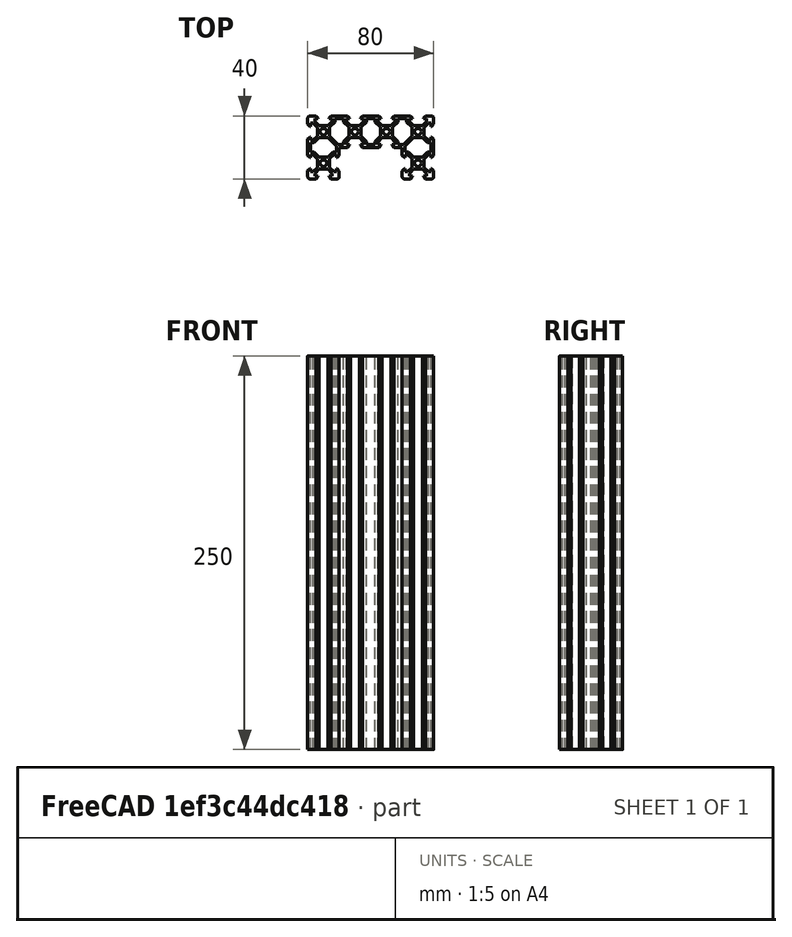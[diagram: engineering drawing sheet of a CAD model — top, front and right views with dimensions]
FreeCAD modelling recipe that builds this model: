
FCSTD DOCUMENT  (FreeCAD 0.15R4671 (Git))
Label: c-beam profile
License: All rights reserved
LicenseURL: http://en.wikipedia.org/wiki/All_rights_reserved
objects: Sketcher::SketchObject×1, Part::Extrusion×1
note: 2 computed .brp shape members not serialized (recipe doc carries the construction recipe); baked Part::Feature solids carry a one-line shape summary decoded from their .brp

FEATURE [Sketcher::SketchObject] Sketch
  sketch-geometry (252):
    g0: LineSegment StartX=57.3 StartY=-18.2 StartZ=0 EndX=57.3 EndY=-16.239 EndZ=0
    g1: LineSegment StartX=57.3 StartY=-16.239 StartZ=0 EndX=53.9 EndY=-12.839 EndZ=0
    g2: LineSegment StartX=53.9 StartY=-12.839 StartZ=0 EndX=53.9 EndY=-7.161 EndZ=0
    g3: LineSegment StartX=53.9 StartY=-7.161 StartZ=0 EndX=57.3 EndY=-3.761 EndZ=0
    g4: LineSegment StartX=57.3 StartY=-3.761 StartZ=0 EndX=57.3 EndY=-1.8 EndZ=0
    g5: LineSegment StartX=57.3 StartY=-1.8 StartZ=0 EndX=60 EndY=-1.8 EndZ=0
    g6: LineSegment StartX=60 StartY=-1.8 StartZ=0 EndX=62.7 EndY=-1.8 EndZ=0
    g7: LineSegment StartX=62.7 StartY=-1.8 StartZ=0 EndX=62.7 EndY=-3.761 EndZ=0
    g8: LineSegment StartX=62.7 StartY=-3.761 StartZ=0 EndX=66.1 EndY=-7.161 EndZ=0
    g9: LineSegment StartX=66.1 StartY=-7.161 StartZ=0 EndX=66.1 EndY=-12.839 EndZ=0
    g10: LineSegment StartX=66.1 StartY=-12.839 StartZ=0 EndX=60.6708 EndY=-18.2 EndZ=0
    g11: LineSegment StartX=60.6708 StartY=-18.2 StartZ=0 EndX=60 EndY=-18.2 EndZ=0
    g12: LineSegment StartX=60 StartY=-18.2 StartZ=0 EndX=57.3 EndY=-18.2 EndZ=0
    g13: LineSegment StartX=20 StartY=-18.2 StartZ=0 EndX=19.3292 EndY=-18.2 EndZ=0
    g14: LineSegment StartX=19.3292 StartY=-18.2 StartZ=0 EndX=13.9 EndY=-12.839 EndZ=0
    g15: LineSegment StartX=13.9 StartY=-12.839 StartZ=0 EndX=13.9 EndY=-7.161 EndZ=0
    g16: LineSegment StartX=13.9 StartY=-7.161 StartZ=0 EndX=17.3 EndY=-3.761 EndZ=0
    g17: LineSegment StartX=17.3 StartY=-3.761 StartZ=0 EndX=17.3 EndY=-1.8 EndZ=0
    g18: LineSegment StartX=17.3 StartY=-1.8 StartZ=0 EndX=20 EndY=-1.8 EndZ=0
    g19: LineSegment StartX=20 StartY=-1.8 StartZ=0 EndX=22.7 EndY=-1.8 EndZ=0
    g20: LineSegment StartX=22.7 StartY=-1.8 StartZ=0 EndX=22.7 EndY=-3.761 EndZ=0
    g21: LineSegment StartX=22.7 StartY=-3.761 StartZ=0 EndX=26.1 EndY=-7.161 EndZ=0
    g22: LineSegment StartX=26.1 StartY=-7.161 StartZ=0 EndX=26.1 EndY=-12.839 EndZ=0
    g23: LineSegment StartX=26.1 StartY=-12.839 StartZ=0 EndX=22.7 EndY=-16.239 EndZ=0
    g24: LineSegment StartX=22.7 StartY=-16.239 StartZ=0 EndX=22.7 EndY=-18.2 EndZ=0
    g25: LineSegment StartX=22.7 StartY=-18.2 StartZ=0 EndX=20 EndY=-18.2 EndZ=0
    g26: ArcOfCircle CenterX=1.5 CenterY=-1.5 CenterZ=0 NormalX=0 NormalY=0 NormalZ=1 Radius=1.5 StartAngle=1.5708 EndAngle=3.14159
    g27: LineSegment StartX=5.114 StartY=0 StartZ=0 EndX=1.5 EndY=0 EndZ=0
    g28: LineSegment StartX=0 StartY=-1.5 StartZ=0 EndX=0 EndY=-5.2509 EndZ=0
    g29: LineSegment StartX=0 StartY=-5.2509 StartZ=0 EndX=1.3621 EndY=-6.613 EndZ=0
    g30: LineSegment StartX=1.3621 StartY=-6.613 StartZ=0 EndX=1.6631 EndY=-6.613 EndZ=0
    g31: LineSegment StartX=1.6631 StartY=-6.613 StartZ=0 EndX=1.6631 EndY=-4.5 EndZ=0
    g32: LineSegment StartX=1.6631 StartY=-4.5 StartZ=0 EndX=3.3021 EndY=-4.5 EndZ=0
    g33: LineSegment StartX=3.3021 StartY=-4.5 StartZ=0 EndX=6.1 EndY=-7.2979 EndZ=0
    g34: LineSegment StartX=6.1 StartY=-7.2979 StartZ=0 EndX=6.1 EndY=-12.7021 EndZ=0
    g35: LineSegment StartX=6.1 StartY=-12.7021 StartZ=0 EndX=3.3021 EndY=-15.5 EndZ=0
    g36: LineSegment StartX=3.3021 StartY=-15.5 StartZ=0 EndX=1.6631 EndY=-15.5 EndZ=0
    g37: LineSegment StartX=1.6631 StartY=-15.5 StartZ=0 EndX=1.6631 EndY=-13.387 EndZ=0
    g38: LineSegment StartX=1.6631 StartY=-13.387 StartZ=0 EndX=1.3621 EndY=-13.387 EndZ=0
    g39: LineSegment StartX=1.3621 StartY=-13.387 StartZ=0 EndX=0 EndY=-14.7491 EndZ=0
    g40: LineSegment StartX=0 StartY=-14.7491 StartZ=0 EndX=0 EndY=-25.2509 EndZ=0
    g41: LineSegment StartX=0 StartY=-25.2509 StartZ=0 EndX=1.3621 EndY=-26.613 EndZ=0
    g42: LineSegment StartX=1.3621 StartY=-26.613 StartZ=0 EndX=1.6631 EndY=-26.613 EndZ=0
    g43: LineSegment StartX=1.6631 StartY=-26.613 StartZ=0 EndX=1.6631 EndY=-24.5 EndZ=0
    g44: LineSegment StartX=1.6631 StartY=-24.5 StartZ=0 EndX=3.3021 EndY=-24.5 EndZ=0
    g45: LineSegment StartX=3.3021 StartY=-24.5 StartZ=0 EndX=6.1 EndY=-27.2979 EndZ=0
    g46: LineSegment StartX=6.1 StartY=-27.2979 StartZ=0 EndX=6.1 EndY=-32.7021 EndZ=0
    g47: LineSegment StartX=6.1 StartY=-32.7021 StartZ=0 EndX=3.3021 EndY=-35.5 EndZ=0
    g48: LineSegment StartX=3.3021 StartY=-35.5 StartZ=0 EndX=1.6631 EndY=-35.5 EndZ=0
    g49: LineSegment StartX=1.6631 StartY=-35.5 StartZ=0 EndX=1.6631 EndY=-33.387 EndZ=0
    g50: LineSegment StartX=1.6631 StartY=-33.387 StartZ=0 EndX=1.3621 EndY=-33.387 EndZ=0
    g51: LineSegment StartX=1.3621 StartY=-33.387 StartZ=0 EndX=0 EndY=-34.7491 EndZ=0
    g52: LineSegment StartX=0 StartY=-34.7491 StartZ=0 EndX=0 EndY=-38.5 EndZ=0
    g53: ArcOfCircle CenterX=1.5 CenterY=-38.5 CenterZ=0 NormalX=0 NormalY=0 NormalZ=1 Radius=1.5 StartAngle=3.14159 EndAngle=4.71239
    g54: LineSegment StartX=1.5 StartY=-40 StartZ=0 EndX=5.114 EndY=-40 EndZ=0
    g55: LineSegment StartX=5.114 StartY=-40 StartZ=0 EndX=6.613 EndY=-38.501 EndZ=0
    g56: LineSegment StartX=6.613 StartY=-38.501 StartZ=0 EndX=6.613 EndY=-38.2 EndZ=0
    g57: LineSegment StartX=6.613 StartY=-38.2 StartZ=0 EndX=4.5 EndY=-38.2 EndZ=0
    g58: LineSegment StartX=4.5 StartY=-38.2 StartZ=0 EndX=4.5 EndY=-36.561 EndZ=0
    g59: LineSegment StartX=4.5 StartY=-36.561 StartZ=0 EndX=7.161 EndY=-33.9 EndZ=0
    g60: LineSegment StartX=7.161 StartY=-33.9 StartZ=0 EndX=12.839 EndY=-33.9 EndZ=0
    g61: LineSegment StartX=12.839 StartY=-33.9 StartZ=0 EndX=15.5 EndY=-36.561 EndZ=0
    g62: LineSegment StartX=15.5 StartY=-36.561 StartZ=0 EndX=15.5 EndY=-38.2 EndZ=0
    g63: LineSegment StartX=15.5 StartY=-38.2 StartZ=0 EndX=13.387 EndY=-38.2 EndZ=0
    g64: LineSegment StartX=13.387 StartY=-38.2 StartZ=0 EndX=13.387 EndY=-38.501 EndZ=0
    g65: LineSegment StartX=13.387 StartY=-38.501 StartZ=0 EndX=14.886 EndY=-40 EndZ=0
    g66: LineSegment StartX=14.886 StartY=-40 StartZ=0 EndX=18.5 EndY=-40 EndZ=0
    g67: ArcOfCircle CenterX=18.5 CenterY=-38.5 CenterZ=0 NormalX=0 NormalY=0 NormalZ=1 Radius=1.5 StartAngle=4.71239 EndAngle=6.28319
    g68: LineSegment StartX=20 StartY=-38.5 StartZ=0 EndX=20 EndY=-34.886 EndZ=0
    g69: LineSegment StartX=20 StartY=-34.886 StartZ=0 EndX=18.501 EndY=-33.387 EndZ=0
    g70: LineSegment StartX=18.501 StartY=-33.387 StartZ=0 EndX=18.2 EndY=-33.387 EndZ=0
    g71: LineSegment StartX=18.2 StartY=-33.387 StartZ=0 EndX=18.2 EndY=-35.5 EndZ=0
    g72: LineSegment StartX=18.2 StartY=-35.5 StartZ=0 EndX=16.561 EndY=-35.5 EndZ=0
    g73: LineSegment StartX=16.561 StartY=-35.5 StartZ=0 EndX=13.9 EndY=-32.839 EndZ=0
    g74: LineSegment StartX=13.9 StartY=-32.839 StartZ=0 EndX=13.9 EndY=-27.161 EndZ=0
    g75: LineSegment StartX=13.9 StartY=-27.161 StartZ=0 EndX=16.561 EndY=-24.5 EndZ=0
    g76: LineSegment StartX=16.561 StartY=-24.5 StartZ=0 EndX=18.2 EndY=-24.5 EndZ=0
    g77: LineSegment StartX=18.2 StartY=-24.5 StartZ=0 EndX=18.2 EndY=-26.613 EndZ=0
    g78: LineSegment StartX=18.2 StartY=-26.613 StartZ=0 EndX=18.501 EndY=-26.613 EndZ=0
    g79: LineSegment StartX=18.501 StartY=-26.613 StartZ=0 EndX=20 EndY=-25.114 EndZ=0
    g80: LineSegment StartX=20 StartY=-25.114 StartZ=0 EndX=20 EndY=-20 EndZ=0
    g81: LineSegment StartX=20 StartY=-20 StartZ=0 EndX=25.114 EndY=-20 EndZ=0
    g82: LineSegment StartX=25.114 StartY=-20 StartZ=0 EndX=26.613 EndY=-18.501 EndZ=0
    g83: LineSegment StartX=26.613 StartY=-18.501 StartZ=0 EndX=26.613 EndY=-18.2 EndZ=0
    g84: LineSegment StartX=26.613 StartY=-18.2 StartZ=0 EndX=24.5 EndY=-18.2 EndZ=0
    g85: LineSegment StartX=24.5 StartY=-18.2 StartZ=0 EndX=24.5 EndY=-16.561 EndZ=0
    g86: LineSegment StartX=24.5 StartY=-16.561 StartZ=0 EndX=27.161 EndY=-13.9 EndZ=0
    g87: LineSegment StartX=27.161 StartY=-13.9 StartZ=0 EndX=32.839 EndY=-13.9 EndZ=0
    g88: LineSegment StartX=32.839 StartY=-13.9 StartZ=0 EndX=35.5 EndY=-16.561 EndZ=0
    g89: LineSegment StartX=35.5 StartY=-16.561 StartZ=0 EndX=35.5 EndY=-18.2 EndZ=0
    g90: LineSegment StartX=35.5 StartY=-18.2 StartZ=0 EndX=33.387 EndY=-18.2 EndZ=0
    g91: LineSegment StartX=33.387 StartY=-18.2 StartZ=0 EndX=33.387 EndY=-18.501 EndZ=0
    g92: LineSegment StartX=33.387 StartY=-18.501 StartZ=0 EndX=34.886 EndY=-20 EndZ=0
    g93: LineSegment StartX=34.886 StartY=-20 StartZ=0 EndX=45.114 EndY=-20 EndZ=0
    g94: LineSegment StartX=45.114 StartY=-20 StartZ=0 EndX=46.613 EndY=-18.501 EndZ=0
    g95: LineSegment StartX=46.613 StartY=-18.501 StartZ=0 EndX=46.613 EndY=-18.2 EndZ=0
    g96: LineSegment StartX=46.613 StartY=-18.2 StartZ=0 EndX=44.5 EndY=-18.2 EndZ=0
    g97: LineSegment StartX=44.5 StartY=-18.2 StartZ=0 EndX=44.5 EndY=-16.561 EndZ=0
    g98: LineSegment StartX=44.5 StartY=-16.561 StartZ=0 EndX=47.161 EndY=-13.9 EndZ=0
    g99: LineSegment StartX=47.161 StartY=-13.9 StartZ=0 EndX=52.839 EndY=-13.9 EndZ=0
    g100: LineSegment StartX=52.839 StartY=-13.9 StartZ=0 EndX=55.5 EndY=-16.561 EndZ=0
    g101: LineSegment StartX=55.5 StartY=-16.561 StartZ=0 EndX=55.5 EndY=-18.2 EndZ=0
    g102: LineSegment StartX=55.5 StartY=-18.2 StartZ=0 EndX=53.387 EndY=-18.2 EndZ=0
    g103: LineSegment StartX=53.387 StartY=-18.2 StartZ=0 EndX=53.387 EndY=-18.501 EndZ=0
    g104: LineSegment StartX=53.387 StartY=-18.501 StartZ=0 EndX=54.886 EndY=-20 EndZ=0
    g105: LineSegment StartX=54.886 StartY=-20 StartZ=0 EndX=54.8918 EndY=-20 EndZ=0
    g106: LineSegment StartX=54.8918 StartY=-20 StartZ=0 EndX=55.1918 EndY=-19.9988 EndZ=0
    g107: LineSegment StartX=55.1918 StartY=-19.9988 StartZ=0 EndX=60 EndY=-20 EndZ=0
    g108: LineSegment StartX=60 StartY=-20 StartZ=0 EndX=60 EndY=-25.114 EndZ=0
    g109: LineSegment StartX=60 StartY=-25.114 StartZ=0 EndX=61.499 EndY=-26.613 EndZ=0
    g110: LineSegment StartX=61.499 StartY=-26.613 StartZ=0 EndX=61.8 EndY=-26.613 EndZ=0
    g111: LineSegment StartX=61.8 StartY=-26.613 StartZ=0 EndX=61.8 EndY=-24.5 EndZ=0
    g112: LineSegment StartX=61.8 StartY=-24.5 StartZ=0 EndX=63.439 EndY=-24.5 EndZ=0
    g113: LineSegment StartX=63.439 StartY=-24.5 StartZ=0 EndX=66.1 EndY=-27.161 EndZ=0
    g114: LineSegment StartX=66.1 StartY=-27.161 StartZ=0 EndX=66.1 EndY=-32.839 EndZ=0
    g115: LineSegment StartX=66.1 StartY=-32.839 StartZ=0 EndX=63.439 EndY=-35.5 EndZ=0
    g116: LineSegment StartX=63.439 StartY=-35.5 StartZ=0 EndX=61.8 EndY=-35.5 EndZ=0
    g117: LineSegment StartX=61.8 StartY=-35.5 StartZ=0 EndX=61.8 EndY=-33.387 EndZ=0
    g118: LineSegment StartX=61.8 StartY=-33.387 StartZ=0 EndX=61.499 EndY=-33.387 EndZ=0
    g119: LineSegment StartX=61.499 StartY=-33.387 StartZ=0 EndX=60 EndY=-34.886 EndZ=0
    g120: LineSegment StartX=60 StartY=-34.886 StartZ=0 EndX=60 EndY=-38.5 EndZ=0
    g121: ArcOfCircle CenterX=61.5 CenterY=-38.5 CenterZ=0 NormalX=0 NormalY=0 NormalZ=1 Radius=1.5 StartAngle=3.14159 EndAngle=4.71239
    g122: LineSegment StartX=61.5 StartY=-40 StartZ=0 EndX=65.114 EndY=-40 EndZ=0
    g123: LineSegment StartX=65.114 StartY=-40 StartZ=0 EndX=66.613 EndY=-38.501 EndZ=0
    g124: LineSegment StartX=66.613 StartY=-38.501 StartZ=0 EndX=66.613 EndY=-38.2 EndZ=0
    g125: LineSegment StartX=66.613 StartY=-38.2 StartZ=0 EndX=64.5 EndY=-38.2 EndZ=0
    g126: LineSegment StartX=64.5 StartY=-38.2 StartZ=0 EndX=64.5 EndY=-36.561 EndZ=0
    g127: LineSegment StartX=64.5 StartY=-36.561 StartZ=0 EndX=67.161 EndY=-33.9 EndZ=0
    g128: LineSegment StartX=67.161 StartY=-33.9 StartZ=0 EndX=72.839 EndY=-33.9 EndZ=0
    g129: LineSegment StartX=72.839 StartY=-33.9 StartZ=0 EndX=75.5 EndY=-36.561 EndZ=0
    g130: LineSegment StartX=75.5 StartY=-36.561 StartZ=0 EndX=75.5 EndY=-38.2 EndZ=0
    g131: LineSegment StartX=75.5 StartY=-38.2 StartZ=0 EndX=73.387 EndY=-38.2 EndZ=0
    g132: LineSegment StartX=73.387 StartY=-38.2 StartZ=0 EndX=73.387 EndY=-38.501 EndZ=0
    g133: LineSegment StartX=73.387 StartY=-38.501 StartZ=0 EndX=74.886 EndY=-40 EndZ=0
    g134: LineSegment StartX=74.886 StartY=-40 StartZ=0 EndX=78.5 EndY=-40 EndZ=0
    g135: ArcOfCircle CenterX=78.5 CenterY=-38.5 CenterZ=0 NormalX=0 NormalY=0 NormalZ=1 Radius=1.5 StartAngle=4.71239 EndAngle=6.28319
    g136: LineSegment StartX=80 StartY=-38.5 StartZ=0 EndX=80 EndY=-34.7491 EndZ=0
    g137: LineSegment StartX=80 StartY=-34.7491 StartZ=0 EndX=78.6379 EndY=-33.387 EndZ=0
    g138: LineSegment StartX=78.6379 StartY=-33.387 StartZ=0 EndX=78.3369 EndY=-33.387 EndZ=0
    g139: LineSegment StartX=78.3369 StartY=-33.387 StartZ=0 EndX=78.3369 EndY=-35.5 EndZ=0
    g140: LineSegment StartX=78.3369 StartY=-35.5 StartZ=0 EndX=76.6979 EndY=-35.5 EndZ=0
    g141: LineSegment StartX=76.6979 StartY=-35.5 StartZ=0 EndX=73.9 EndY=-32.7021 EndZ=0
    g142: LineSegment StartX=73.9 StartY=-32.7021 StartZ=0 EndX=73.9 EndY=-27.2979 EndZ=0
    g143: LineSegment StartX=73.9 StartY=-27.2979 StartZ=0 EndX=76.6979 EndY=-24.5 EndZ=0
    g144: LineSegment StartX=76.6979 StartY=-24.5 StartZ=0 EndX=78.3369 EndY=-24.5 EndZ=0
    g145: LineSegment StartX=78.3369 StartY=-24.5 StartZ=0 EndX=78.3369 EndY=-26.613 EndZ=0
    g146: LineSegment StartX=78.3369 StartY=-26.613 StartZ=0 EndX=78.6379 EndY=-26.613 EndZ=0
    g147: LineSegment StartX=78.6379 StartY=-26.613 StartZ=0 EndX=80 EndY=-25.2509 EndZ=0
    g148: LineSegment StartX=80 StartY=-25.2509 StartZ=0 EndX=80 EndY=-14.7491 EndZ=0
    g149: LineSegment StartX=80 StartY=-14.7491 StartZ=0 EndX=78.6379 EndY=-13.387 EndZ=0
    g150: LineSegment StartX=78.6379 StartY=-13.387 StartZ=0 EndX=78.3369 EndY=-13.387 EndZ=0
    g151: LineSegment StartX=78.3369 StartY=-13.387 StartZ=0 EndX=78.3369 EndY=-15.5 EndZ=0
    g152: LineSegment StartX=78.3369 StartY=-15.5 StartZ=0 EndX=76.6979 EndY=-15.5 EndZ=0
    g153: LineSegment StartX=76.6979 StartY=-15.5 StartZ=0 EndX=73.9 EndY=-12.7021 EndZ=0
    g154: LineSegment StartX=73.9 StartY=-12.7021 StartZ=0 EndX=73.9 EndY=-7.2979 EndZ=0
    g155: LineSegment StartX=73.9 StartY=-7.2979 StartZ=0 EndX=76.6979 EndY=-4.5 EndZ=0
    g156: LineSegment StartX=76.6979 StartY=-4.5 StartZ=0 EndX=78.3369 EndY=-4.5 EndZ=0
    g157: LineSegment StartX=78.3369 StartY=-4.5 StartZ=0 EndX=78.3369 EndY=-6.613 EndZ=0
    g158: LineSegment StartX=78.3369 StartY=-6.613 StartZ=0 EndX=78.6379 EndY=-6.613 EndZ=0
    g159: LineSegment StartX=78.6379 StartY=-6.613 StartZ=0 EndX=80 EndY=-5.2509 EndZ=0
    g160: LineSegment StartX=80 StartY=-5.2509 StartZ=0 EndX=80 EndY=-1.5 EndZ=0
    g161: ArcOfCircle CenterX=78.5 CenterY=-1.5 CenterZ=0 NormalX=0 NormalY=0 NormalZ=1 Radius=1.5 StartAngle=0 EndAngle=1.5708
    g162: LineSegment StartX=78.5 StartY=0 StartZ=0 EndX=74.886 EndY=0 EndZ=0
    g163: LineSegment StartX=74.886 StartY=0 StartZ=0 EndX=73.387 EndY=-1.499 EndZ=0
    g164: LineSegment StartX=73.387 StartY=-1.499 StartZ=0 EndX=73.387 EndY=-1.8 EndZ=0
    g165: LineSegment StartX=73.387 StartY=-1.8 StartZ=0 EndX=75.5 EndY=-1.8 EndZ=0
    g166: LineSegment StartX=75.5 StartY=-1.8 StartZ=0 EndX=75.5 EndY=-3.439 EndZ=0
    g167: LineSegment StartX=75.5 StartY=-3.439 StartZ=0 EndX=72.839 EndY=-6.1 EndZ=0
    g168: LineSegment StartX=72.839 StartY=-6.1 StartZ=0 EndX=67.161 EndY=-6.1 EndZ=0
    g169: LineSegment StartX=67.161 StartY=-6.1 StartZ=0 EndX=64.5 EndY=-3.439 EndZ=0
    g170: LineSegment StartX=64.5 StartY=-3.439 StartZ=0 EndX=64.5 EndY=-1.8 EndZ=0
    g171: LineSegment StartX=64.5 StartY=-1.8 StartZ=0 EndX=66.613 EndY=-1.8 EndZ=0
    g172: LineSegment StartX=66.613 StartY=-1.8 StartZ=0 EndX=66.613 EndY=-1.499 EndZ=0
    g173: LineSegment StartX=66.613 StartY=-1.499 StartZ=0 EndX=65.114 EndY=0 EndZ=0
    g174: LineSegment StartX=65.114 StartY=0 StartZ=0 EndX=54.886 EndY=0 EndZ=0
    g175: LineSegment StartX=54.886 StartY=0 StartZ=0 EndX=53.387 EndY=-1.499 EndZ=0
    g176: LineSegment StartX=53.387 StartY=-1.499 StartZ=0 EndX=53.387 EndY=-1.8 EndZ=0
    g177: LineSegment StartX=53.387 StartY=-1.8 StartZ=0 EndX=55.5 EndY=-1.8 EndZ=0
    g178: LineSegment StartX=55.5 StartY=-1.8 StartZ=0 EndX=55.5 EndY=-3.439 EndZ=0
    g179: LineSegment StartX=55.5 StartY=-3.439 StartZ=0 EndX=52.839 EndY=-6.1 EndZ=0
    g180: LineSegment StartX=52.839 StartY=-6.1 StartZ=0 EndX=47.161 EndY=-6.1 EndZ=0
    g181: LineSegment StartX=47.161 StartY=-6.1 StartZ=0 EndX=44.5 EndY=-3.439 EndZ=0
    g182: LineSegment StartX=44.5 StartY=-3.439 StartZ=0 EndX=44.5 EndY=-1.8 EndZ=0
    g183: LineSegment StartX=44.5 StartY=-1.8 StartZ=0 EndX=46.613 EndY=-1.8 EndZ=0
    g184: LineSegment StartX=46.613 StartY=-1.8 StartZ=0 EndX=46.613 EndY=-1.499 EndZ=0
    g185: LineSegment StartX=46.613 StartY=-1.499 StartZ=0 EndX=45.114 EndY=0 EndZ=0
    g186: LineSegment StartX=45.114 StartY=0 StartZ=0 EndX=34.886 EndY=0 EndZ=0
    g187: LineSegment StartX=34.886 StartY=0 StartZ=0 EndX=33.387 EndY=-1.499 EndZ=0
    g188: LineSegment StartX=33.387 StartY=-1.499 StartZ=0 EndX=33.387 EndY=-1.8 EndZ=0
    g189: LineSegment StartX=33.387 StartY=-1.8 StartZ=0 EndX=35.5 EndY=-1.8 EndZ=0
    g190: LineSegment StartX=35.5 StartY=-1.8 StartZ=0 EndX=35.5 EndY=-3.439 EndZ=0
    g191: LineSegment StartX=35.5 StartY=-3.439 StartZ=0 EndX=32.839 EndY=-6.1 EndZ=0
    g192: LineSegment StartX=32.839 StartY=-6.1 StartZ=0 EndX=27.161 EndY=-6.1 EndZ=0
    g193: LineSegment StartX=27.161 StartY=-6.1 StartZ=0 EndX=24.5 EndY=-3.439 EndZ=0
    g194: LineSegment StartX=24.5 StartY=-3.439 StartZ=0 EndX=24.5 EndY=-1.8 EndZ=0
    g195: LineSegment StartX=24.5 StartY=-1.8 StartZ=0 EndX=26.613 EndY=-1.8 EndZ=0
    g196: LineSegment StartX=26.613 StartY=-1.8 StartZ=0 EndX=26.613 EndY=-1.499 EndZ=0
    g197: LineSegment StartX=26.613 StartY=-1.499 StartZ=0 EndX=25.114 EndY=0 EndZ=0
    g198: LineSegment StartX=25.114 StartY=0 StartZ=0 EndX=14.886 EndY=0 EndZ=0
    g199: LineSegment StartX=14.886 StartY=0 StartZ=0 EndX=13.387 EndY=-1.499 EndZ=0
    g200: LineSegment StartX=13.387 StartY=-1.499 StartZ=0 EndX=13.387 EndY=-1.8 EndZ=0
    g201: LineSegment StartX=13.387 StartY=-1.8 StartZ=0 EndX=15.5 EndY=-1.8 EndZ=0
    g202: LineSegment StartX=15.5 StartY=-1.8 StartZ=0 EndX=15.5 EndY=-3.439 EndZ=0
    g203: LineSegment StartX=15.5 StartY=-3.439 StartZ=0 EndX=12.839 EndY=-6.1 EndZ=0
    g204: LineSegment StartX=12.839 StartY=-6.1 StartZ=0 EndX=7.161 EndY=-6.1 EndZ=0
    g205: LineSegment StartX=7.161 StartY=-6.1 StartZ=0 EndX=4.5 EndY=-3.439 EndZ=0
    g206: LineSegment StartX=4.5 StartY=-3.439 StartZ=0 EndX=4.5 EndY=-1.8 EndZ=0
    g207: LineSegment StartX=4.5 StartY=-1.8 StartZ=0 EndX=6.613 EndY=-1.8 EndZ=0
    g208: LineSegment StartX=6.613 StartY=-1.8 StartZ=0 EndX=6.613 EndY=-1.499 EndZ=0
    g209: LineSegment StartX=6.613 StartY=-1.499 StartZ=0 EndX=5.114 EndY=0 EndZ=0
    g210: Circle CenterX=10 CenterY=-30 CenterZ=0 NormalX=0 NormalY=0 NormalZ=-1 Radius=2.1
    g211: Circle CenterX=70 CenterY=-30 CenterZ=0 NormalX=0 NormalY=0 NormalZ=-1 Radius=2.1
    g212: Circle CenterX=70 CenterY=-10 CenterZ=0 NormalX=0 NormalY=0 NormalZ=-1 Radius=2.1
    g213: Circle CenterX=10 CenterY=-10 CenterZ=0 NormalX=0 NormalY=0 NormalZ=-1 Radius=2.1
    g214: Circle CenterX=30 CenterY=-10 CenterZ=0 NormalX=0 NormalY=0 NormalZ=-1 Radius=2.1
    g215: Circle CenterX=50 CenterY=-10 CenterZ=0 NormalX=0 NormalY=0 NormalZ=-1 Radius=2.1
    g216: LineSegment StartX=42.7156 StartY=-3.79115 StartZ=0 EndX=46.1296 EndY=-7.17706 EndZ=0
    g217: LineSegment StartX=46.1296 StartY=-7.17706 StartZ=0 EndX=46.1531 EndY=-12.855 EndZ=0
    g218: LineSegment StartX=46.1531 StartY=-12.855 StartZ=0 EndX=42.7672 EndY=-16.269 EndZ=0
    g219: LineSegment StartX=42.7672 StartY=-16.269 StartZ=0 EndX=42.7753 EndY=-18.23 EndZ=0
    g220: LineSegment StartX=42.7753 StartY=-18.23 StartZ=0 EndX=39.9247 EndY=-18.2412 EndZ=0
    g221: LineSegment StartX=39.9247 StartY=-18.2412 StartZ=0 EndX=37.2247 EndY=-18.23 EndZ=0
    g222: LineSegment StartX=37.2247 StartY=-18.23 StartZ=0 EndX=37.2328 EndY=-16.269 EndZ=0
    g223: LineSegment StartX=37.2328 StartY=-16.269 StartZ=0 EndX=33.8469 EndY=-12.855 EndZ=0
    g224: LineSegment StartX=33.8469 StartY=-12.855 StartZ=0 EndX=33.8704 EndY=-7.17706 EndZ=0
    g225: LineSegment StartX=33.8704 StartY=-7.17706 StartZ=0 EndX=37.2844 EndY=-3.79115 EndZ=0
    g226: LineSegment StartX=37.2844 StartY=-3.79115 StartZ=0 EndX=37.2925 EndY=-1.83017 EndZ=0
    g227: LineSegment StartX=37.2925 StartY=-1.83017 StartZ=0 EndX=39.9925 EndY=-1.84133 EndZ=0
    g228: LineSegment StartX=39.9925 StartY=-1.84133 StartZ=0 EndX=42.7075 EndY=-1.83017 EndZ=0
    g229: LineSegment StartX=42.7075 StartY=-1.83017 StartZ=0 EndX=42.7156 EndY=-3.79115 EndZ=0
    g230: LineSegment StartX=15.939 StartY=-23 StartZ=0 EndX=12.839 EndY=-26.1 EndZ=0
    g231: LineSegment StartX=12.839 StartY=-26.1 StartZ=0 EndX=7.161 EndY=-26.1 EndZ=0
    g232: LineSegment StartX=7.161 StartY=-26.1 StartZ=0 EndX=4.061 EndY=-23 EndZ=0
    g233: LineSegment StartX=4.061 StartY=-23 StartZ=0 EndX=1.6631 EndY=-23 EndZ=0
    g234: LineSegment StartX=1.6631 StartY=-23 StartZ=0 EndX=1.6631 EndY=-17 EndZ=0
    g235: LineSegment StartX=1.6631 StartY=-17 StartZ=0 EndX=4.061 EndY=-17 EndZ=0
    g236: LineSegment StartX=4.061 StartY=-17 StartZ=0 EndX=7.161 EndY=-13.9 EndZ=0
    g237: LineSegment StartX=7.161 StartY=-13.9 StartZ=0 EndX=12.839 EndY=-13.9 EndZ=0
    g238: LineSegment StartX=12.839 StartY=-13.9 StartZ=0 EndX=18.2 EndY=-19.261 EndZ=0
    g239: LineSegment StartX=18.2 StartY=-19.261 StartZ=0 EndX=18.2 EndY=-23 EndZ=0
    g240: LineSegment StartX=18.2 StartY=-23 StartZ=0 EndX=15.939 EndY=-23 EndZ=0
    g241: LineSegment StartX=78.3369 StartY=-23 StartZ=0 EndX=75.939 EndY=-23 EndZ=0
    g242: LineSegment StartX=75.939 StartY=-23 StartZ=0 EndX=72.839 EndY=-26.1 EndZ=0
    g243: LineSegment StartX=72.839 StartY=-26.1 StartZ=0 EndX=67.161 EndY=-26.1 EndZ=0
    g244: LineSegment StartX=67.161 StartY=-26.1 StartZ=0 EndX=64.061 EndY=-23 EndZ=0
    g245: LineSegment StartX=64.061 StartY=-23 StartZ=0 EndX=61.8 EndY=-23 EndZ=0
    g246: LineSegment StartX=61.8 StartY=-23 StartZ=0 EndX=61.8 EndY=-19.261 EndZ=0
    g247: LineSegment StartX=61.8 StartY=-19.261 StartZ=0 EndX=67.161 EndY=-13.9 EndZ=0
    g248: LineSegment StartX=67.161 StartY=-13.9 StartZ=0 EndX=72.839 EndY=-13.9 EndZ=0
    g249: LineSegment StartX=72.839 StartY=-13.9 StartZ=0 EndX=75.939 EndY=-17 EndZ=0
    g250: LineSegment StartX=75.939 StartY=-17 StartZ=0 EndX=78.3369 EndY=-17 EndZ=0
    g251: LineSegment StartX=78.3369 StartY=-17 StartZ=0 EndX=78.3369 EndY=-23 EndZ=0
FEATURE [Part::Extrusion] Extrude001
  Base = -> Sketch
  Dir = (0,0,250)
  Solid = false
